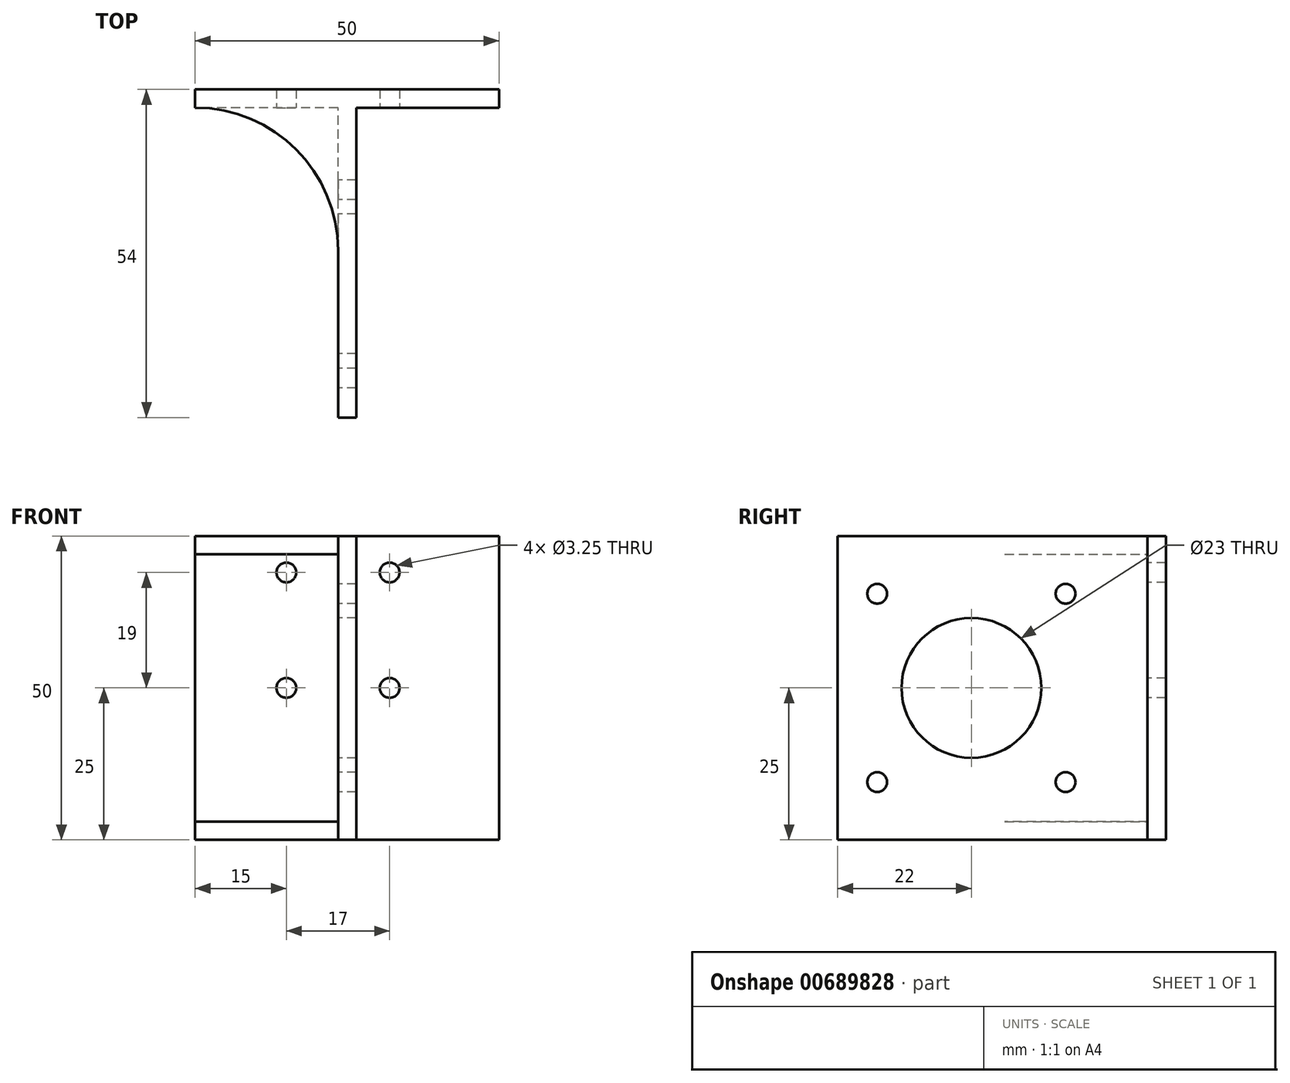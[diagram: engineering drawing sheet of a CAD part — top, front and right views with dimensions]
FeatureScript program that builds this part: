
annotation { "Feature Type Name" : "Feature", "Feature Type Description" : "" }
export const myFeature = defineFeature(function(context is Context, id is Id, definition is map)
    precondition{}
    {
        {
            var Q0;
            Q0=qCreatedBy(makeId("Right.planeOp"),FACE);
            var sketch = newSketch(context, id + "F0", { "sketchPlane" : qUnion([Q0])});
            skCircle(sketch, "E0", {"center": v(0, 0) * mm, "radius": 11.5 * mm});
            skCircle(sketch, "E1", {"center": v(15.5, 15.5) * mm, "radius": 1.63 * mm});
            skCircle(sketch, "E2", {"center": v(15.5, -15.5) * mm, "radius": 1.63 * mm});
            skCircle(sketch, "E3", {"center": v(-15.5, -15.5) * mm, "radius": 1.63 * mm});
            skCircle(sketch, "E4", {"center": v(-15.5, 15.5) * mm, "radius": 1.63 * mm});
            skLineSegment(sketch, "E5.bottom", {"start": v(-22, 25) * mm, "end": v(29, 25) * mm});
            skLineSegment(sketch, "E5.top", {"start": v(-22, -25) * mm, "end": v(29, -25) * mm});
            skLineSegment(sketch, "E5.left", {"start": v(-22, 25) * mm, "end": v(-22, -25) * mm});
            skLineSegment(sketch, "E5.right", {"start": v(29, 25) * mm, "end": v(29, -25) * mm});
            skSolve(sketch);
        }
        {
            var Q0;
            Q0=makeQuery(id+"F0.imprint","IMPRINT",FACE,{"disambiguationData":[TD([[makeQuery(id+"F0.imprint","IMPRINT",EDGE,{"derivedFrom":sQuery(id+"F0.wireOp",EDGE,"E0")}),-1.0]])]});
            extrude(context, id + "F1", {"entities" : qUnion([Q0]), "endBound" : BoundingType.SYMMETRIC, "depth" : 3 * mm, "offsetDistance" : 25 * mm});
        }
        {
            var Q0;
            Q0=makeQuery(id+"F1.opExtrude","SWEPT_FACE",FACE,{"disambiguationData":[OSD([sQuery(id+"F0.wireOp",EDGE,"E5.right")])]});
            var sketch = newSketch(context, id + "F2", { "sketchPlane" : qUnion([Q0])});
            skCircle(sketch, "E6", {"center": v(-7, 0) * mm, "radius": 1.63 * mm});
            skCircle(sketch, "E7", {"center": v(-7, 19) * mm, "radius": 1.63 * mm});
            skCircle(sketch, "E8", {"center": v(10, 19) * mm, "radius": 1.63 * mm});
            skCircle(sketch, "E9", {"center": v(10, 0) * mm, "radius": 1.63 * mm});
            skLineSegment(sketch, "E10", {"start": v(0, 10.56) * mm, "end": v(0, -23.23) * mm, "construction": true});
            skLineSegment(sketch, "E11.bottom", {"start": v(25, 25) * mm, "end": v(-25, 25) * mm});
            skLineSegment(sketch, "E11.top", {"start": v(25, -25) * mm, "end": v(-25, -25) * mm});
            skLineSegment(sketch, "E11.left", {"start": v(25, 25) * mm, "end": v(25, -25) * mm});
            skLineSegment(sketch, "E11.right", {"start": v(-25, 25) * mm, "end": v(-25, -25) * mm});
            skSolve(sketch);
        }
        {
            var Q0;
            Q0=qSketchRegion(id+"F2",true);
            extrude(context, id + "F3", {"entities" : qUnion([Q0]), "operationType" : NewBodyOperationType.ADD, "depth" : 3 * mm, "offsetDistance" : 25 * mm});
        }
        {
            var Q0;
            Q0=makeQuery(id+"F3.boolean.opBoolean","MERGE",FACE,{"derivedFrom":[makeQuery(id+"F1.opExtrude","SWEPT_FACE",FACE,{"disambiguationData":[OSD([sQuery(id+"F0.wireOp",EDGE,"E5.top")])]}),makeQuery(id+"F3.opExtrude","SWEPT_FACE",FACE,{"disambiguationData":[OSD([sQuery(id+"F2.wireOp",EDGE,"E11.top")])]})]});
            var sketch = newSketch(context, id + "F4", { "sketchPlane" : qUnion([Q0])});
            skArc(sketch, "E12", {"start": v(-25, -29) * mm, "mid": v(-8.38, -22.12) * mm, "end": v(-1.5, -5.5) * mm});
            skLineSegment(sketch, "E13", {"start": v(-1.5, -5.5) * mm, "end": v(-1.5, -29) * mm});
            skLineSegment(sketch, "E14", {"start": v(-1.5, -29) * mm, "end": v(-25, -29) * mm});
            skSolve(sketch);
        }
        {
            var Q0;
            Q0=makeQuery(id+"F3.boolean.opBoolean","MERGE",FACE,{"derivedFrom":[makeQuery(id+"F1.opExtrude","SWEPT_FACE",FACE,{"disambiguationData":[OSD([sQuery(id+"F0.wireOp",EDGE,"E5.bottom")])]}),makeQuery(id+"F3.opExtrude","SWEPT_FACE",FACE,{"disambiguationData":[OSD([sQuery(id+"F2.wireOp",EDGE,"E11.bottom")])]})]});
            var sketch = newSketch(context, id + "F5", { "sketchPlane" : qUnion([Q0])});
            skArc(sketch, "E15", {"start": v(-1.5, 5.5) * mm, "mid": v(-8.38, 22.12) * mm, "end": v(-25, 29) * mm});
            skLineSegment(sketch, "E16", {"start": v(-1.5, 29) * mm, "end": v(-25, 29) * mm});
            skSolve(sketch);
        }
        {
            var Q0;
            {var subQ0=sQuery(id+"F5.wireOp",EDGE,"E15");Q0=makeQuery(id+"F5.imprint","IMPRINT",FACE,{"disambiguationData":[TD([[makeQuery(id+"F5.imprint","IMPRINT",EDGE,{"derivedFrom":subQ0}),-1.0]])]});}
            extrude(context, id + "F6", {"entities" : qUnion([Q0]), "operationType" : NewBodyOperationType.ADD, "depth" : -3 * mm, "offsetDistance" : 25 * mm});
        }
        {
            var Q0;
            Q0=makeQuery(id+"F4.imprint","IMPRINT",FACE,{"disambiguationData":[TD([[makeQuery(id+"F4.imprint","IMPRINT",EDGE,{"derivedFrom":sQuery(id+"F4.wireOp",EDGE,"E12")}),-1.0]])]});
            extrude(context, id + "F7", {"entities" : qUnion([Q0]), "operationType" : NewBodyOperationType.ADD, "depth" : -3 * mm, "offsetDistance" : 25 * mm});
        }
    });
